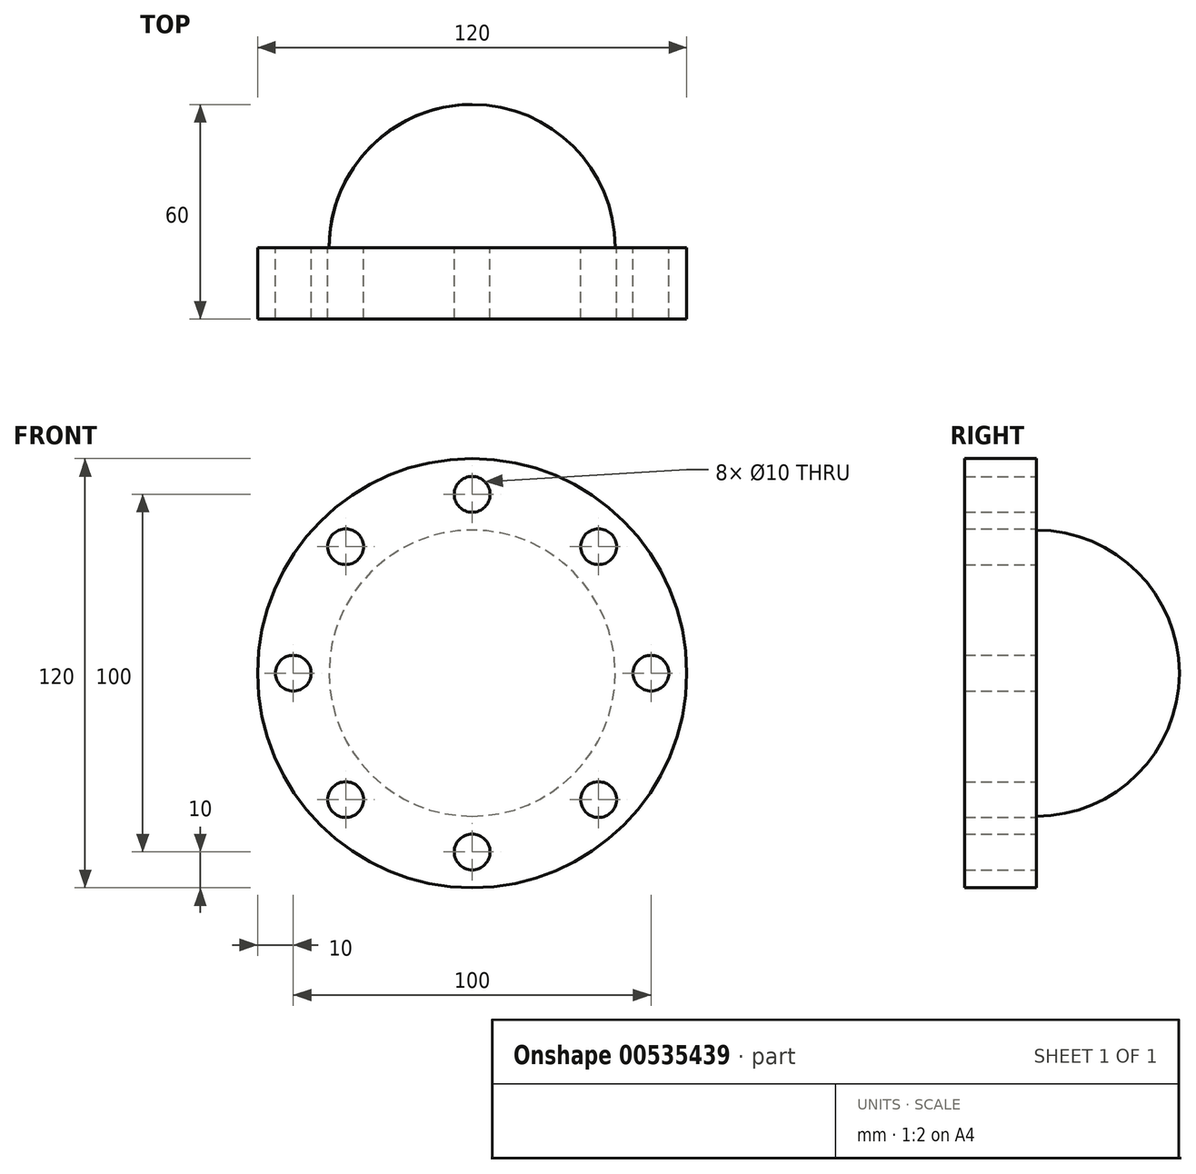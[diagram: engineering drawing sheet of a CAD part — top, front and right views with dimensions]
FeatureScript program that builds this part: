
annotation { "Feature Type Name" : "Feature", "Feature Type Description" : "" }
export const myFeature = defineFeature(function(context is Context, id is Id, definition is map)
    precondition{}
    {
        {
            var Q0;
            Q0=qCreatedBy(makeId("Front.planeOp"),FACE);
            var sketch = newSketch(context, id + "F0", { "sketchPlane" : qUnion([Q0])});
            skCircle(sketch, "E0", {"center": v(0, 0) * mm, "radius": 60 * mm});
            skCircle(sketch, "E1", {"center": v(0, 50) * mm, "radius": 5 * mm});
            skCircle(sketch, "E2.1.0", {"center": v(-35.36, 35.36) * mm, "radius": 5 * mm});
            skCircle(sketch, "E2.2.0", {"center": v(-50, 0) * mm, "radius": 5 * mm});
            skCircle(sketch, "E2.3.0", {"center": v(-35.36, -35.36) * mm, "radius": 5 * mm});
            skCircle(sketch, "E2.4.0", {"center": v(0, -50) * mm, "radius": 5 * mm});
            skCircle(sketch, "E2.5.0", {"center": v(35.36, -35.36) * mm, "radius": 5 * mm});
            skCircle(sketch, "E2.6.0", {"center": v(50, 0) * mm, "radius": 5 * mm});
            skCircle(sketch, "E2.7.0", {"center": v(35.36, 35.36) * mm, "radius": 5 * mm});
            skSolve(sketch);
        }
        {
            var Q0;
            Q0 = qSketchRegion(id + "F0", true);
            extrude(context, id + "F1", {"entities" : qUnion([Q0]), "depth" : 20 * mm, "offsetDistance" : 25 * mm});
        }
        {
            var Q0;
            Q0=qCreatedBy(makeId("Top.planeOp"),FACE);
            var sketch = newSketch(context, id + "F2", { "sketchPlane" : qUnion([Q0])});
            skArc(sketch, "E3", {"start": v(0, 40) * mm, "mid": v(-28.28, 28.28) * mm, "end": v(-40, 0) * mm});
            skLineSegment(sketch, "E4", {"start": v(0, 0) * mm, "end": v(0, 40) * mm});
            skLineSegment(sketch, "E5.trimOffspring", {"start": v(0, 0) * mm, "end": v(-40, 0) * mm});
            skPoint(sketch, "E6.0.start.orphan", {"position": v(60, 0) * mm});
            skPoint(sketch, "E7.orphan", {"position": v(-60, 0) * mm});
            skSolve(sketch);
        }
        {
            var Q0;
            Q0 = qSketchRegion(id + "F2", true);
            var Q1;
            Q1=sQuery(id+"F2.wireOp",EDGE,"E4");
            revolve(context, id + "F3", {"operationType" : NewBodyOperationType.ADD, "entities" : qUnion([Q0]), "axis" : qUnion([Q1]), "revolveType" : RevolveType.FULL});
        }
    });
